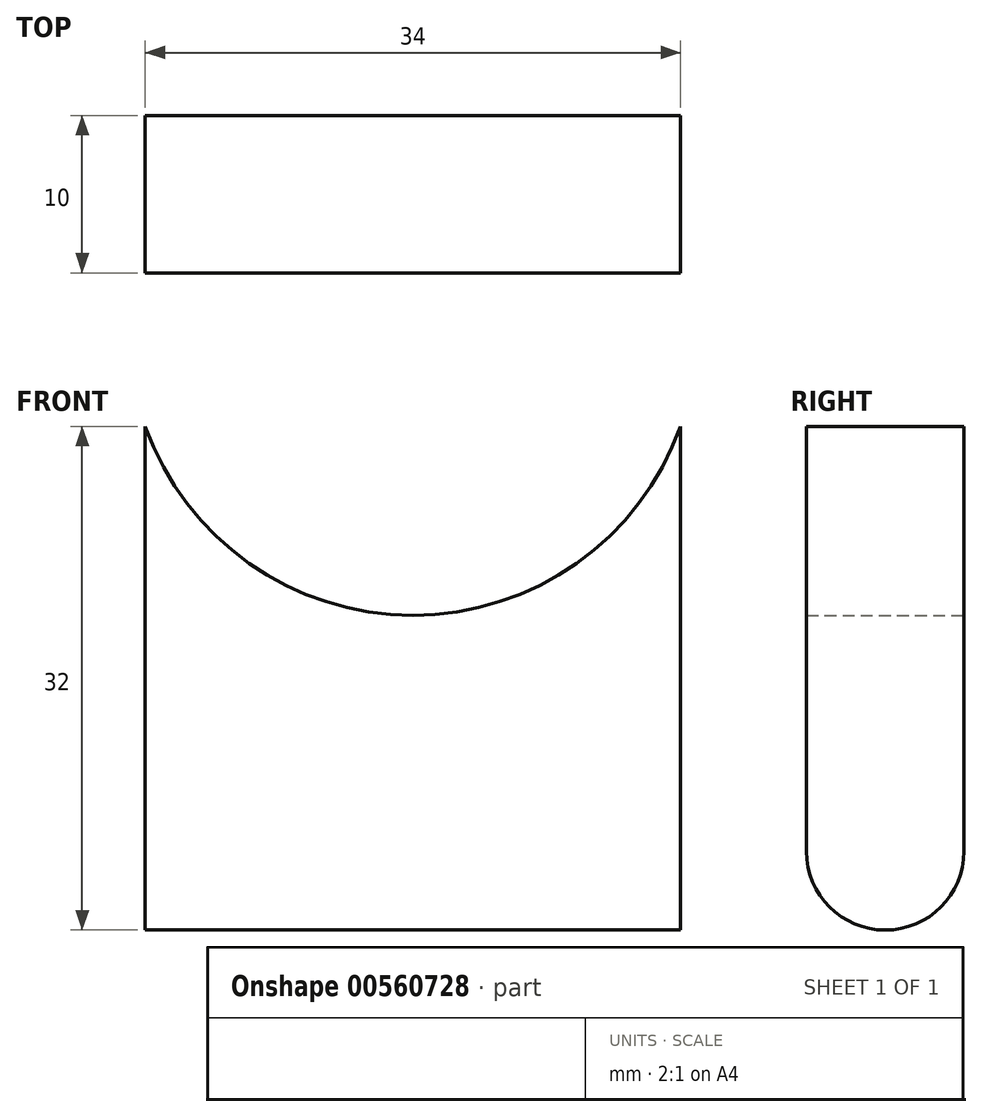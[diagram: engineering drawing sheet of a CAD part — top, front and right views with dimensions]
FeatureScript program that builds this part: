
annotation { "Feature Type Name" : "Feature", "Feature Type Description" : "" }
export const myFeature = defineFeature(function(context is Context, id is Id, definition is map)
    precondition{}
    {
        {
            var Q0;
            Q0=qCreatedBy(makeId("Front.planeOp"),FACE);
            var sketch = newSketch(context, id + "F0", { "sketchPlane" : qUnion([Q0])});
            skLineSegment(sketch, "E0.bottom", {"start": v(5, 0) * mm, "end": v(34, 0) * mm});
            skLineSegment(sketch, "E0.top", {"start": v(0, -32) * mm, "end": v(34, -32) * mm});
            skLineSegment(sketch, "E0.left", {"start": v(0, -5) * mm, "end": v(0, -32) * mm});
            skLineSegment(sketch, "E0.right", {"start": v(34, 0) * mm, "end": v(34, -32) * mm});
            skLineSegment(sketch, "E1", {"start": v(0, 0) * mm, "end": v(0, -12) * mm, "construction": true});
            skLineSegment(sketch, "E2", {"start": v(0, -12) * mm, "end": v(17, -12) * mm, "construction": true});
            skPoint(sketch, "E3.visualSharp", {"position": v(0, 0) * mm});
            skArc(sketch, "E4", {"start": v(17, -12) * mm, "mid": v(27.4, -8.7) * mm, "end": v(34, 0) * mm});
            skArc(sketch, "E5", {"start": v(0, 0) * mm, "mid": v(6.6, -8.7) * mm, "end": v(17, -12) * mm});
            skLineSegment(sketch, "E6.bottom", {"start": v(0, 0) * mm, "end": v(34, 0) * mm});
            skLineSegment(sketch, "E6.left", {"start": v(0, 0) * mm, "end": v(0, -32) * mm});
            skSolve(sketch);
        }
        {
            var Q0;
            Q0=makeQuery(id+"F0.imprint","IMPRINT",FACE,{"disambiguationData":[TD([[makeQuery(id+"F0.imprint","IMPRINT",EDGE,{"derivedFrom":sQuery(id+"F0.wireOp",EDGE,"E4")}),-1.0]])]});
            extrude(context, id + "F1", {"entities" : qUnion([Q0]), "depth" : 10 * mm, "offsetDistance" : 25 * mm});
        }
        {
            var Q0;
            Q0=makeQuery(id+"F1.opExtrude","CAP_EDGE",EDGE,{"disambiguationData":[OSD([sQuery(id+"F0.wireOp",EDGE,"E0.top")])],"isStart":true});
            var Q1;
            Q1=makeQuery(id+"F1.opExtrude","CAP_EDGE",EDGE,{"disambiguationData":[OSD([sQuery(id+"F0.wireOp",EDGE,"E0.top")])],"isStart":false});
            fillet(context, id + "F2", {"entities" : qUnion([Q0, Q1]), "radius" : 5 * mm, "tangentPropagation" : true, "allowEdgeOverflow" : false});
        }
    });
